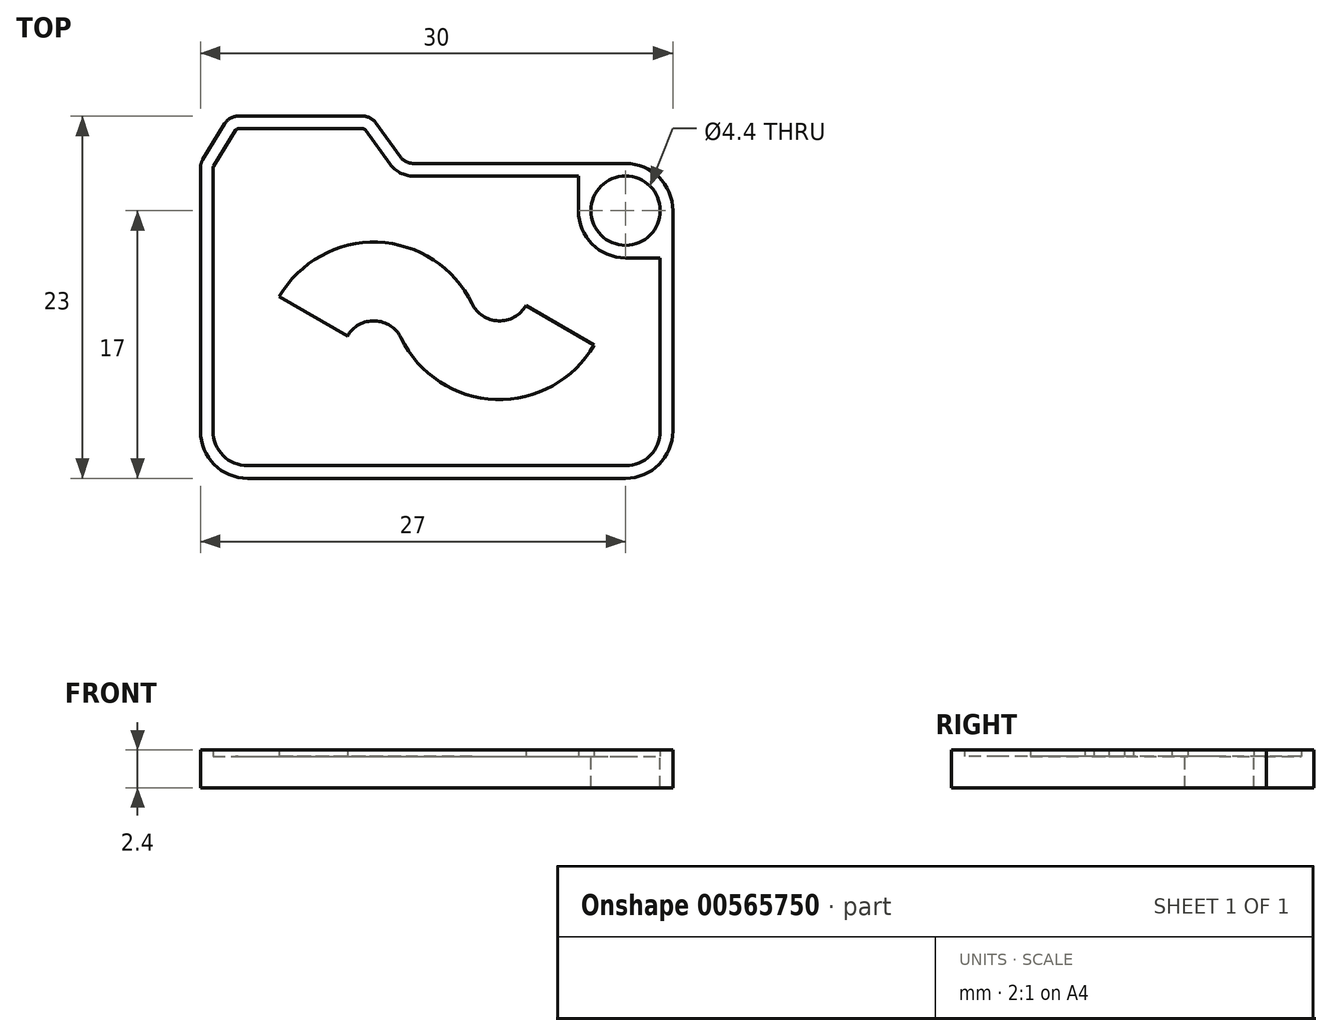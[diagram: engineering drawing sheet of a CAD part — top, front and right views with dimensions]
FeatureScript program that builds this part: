
annotation { "Feature Type Name" : "Feature", "Feature Type Description" : "" }
export const myFeature = defineFeature(function(context is Context, id is Id, definition is map)
    precondition{}
    {
        {
            var Q0;
            Q0=qCreatedBy(makeId("Top.planeOp"),FACE);
            var sketch = newSketch(context, id + "F0", { "sketchPlane" : qUnion([Q0])});
            skLineSegment(sketch, "E0.bottom", {"start": v(-1.49, 10) * mm, "end": v(12, 10) * mm});
            skLineSegment(sketch, "E0.top", {"start": v(-12, -10) * mm, "end": v(12, -10) * mm});
            skLineSegment(sketch, "E0.left", {"start": v(-15, 9.72) * mm, "end": v(-15, -7) * mm});
            skLineSegment(sketch, "E0.right", {"start": v(15, 7) * mm, "end": v(15, -7) * mm});
            skPoint(sketch, "E0.middle", {"position": v(0, 0) * mm});
            skLineSegment(sketch, "E1", {"start": v(-14.85, 10.24) * mm, "end": v(-13.46, 12.52) * mm});
            skLineSegment(sketch, "E2", {"start": v(-12.6, 13) * mm, "end": v(-4.68, 13) * mm});
            skLineSegment(sketch, "E3", {"start": v(-3.86, 12.58) * mm, "end": v(-2.3, 10.42) * mm});
            skArc(sketch, "E4", {"start": v(-2.25, -1.1) * mm, "mid": v(-3.92, 0) * mm, "end": v(-5.67, -0.97) * mm});
            skArc(sketch, "E5", {"start": v(2.25, 1.1) * mm, "mid": v(-3.74, 5) * mm, "end": v(-10, 1.53) * mm});
            skArc(sketch, "E6", {"start": v(-2.25, -1.1) * mm, "mid": v(3.74, -5) * mm, "end": v(10, -1.53) * mm});
            skArc(sketch, "E7", {"start": v(2.25, 1.1) * mm, "mid": v(3.92, 0) * mm, "end": v(5.67, 0.97) * mm});
            skLineSegment(sketch, "E8", {"start": v(-5.67, -0.97) * mm, "end": v(-10, 1.53) * mm});
            skLineSegment(sketch, "E9", {"start": v(5.67, 0.97) * mm, "end": v(10, -1.53) * mm});
            skPoint(sketch, "E10.visualSharp", {"position": v(15, 10) * mm});
            skArc(sketch, "E10.filletArc", {"start": v(15, 7) * mm, "mid": v(14.12, 9.12) * mm, "end": v(12, 10) * mm});
            skPoint(sketch, "E11.visualSharp", {"position": v(15, -10) * mm});
            skArc(sketch, "E11.filletArc", {"start": v(12, -10) * mm, "mid": v(14.12, -9.12) * mm, "end": v(15, -7) * mm});
            skPoint(sketch, "E12.visualSharp", {"position": v(-15, -10) * mm});
            skArc(sketch, "E12.filletArc", {"start": v(-15, -7) * mm, "mid": v(-14.12, -9.12) * mm, "end": v(-12, -10) * mm});
            skPoint(sketch, "E13.visualSharp", {"position": v(-15, 10) * mm});
            skArc(sketch, "E13.filletArc", {"start": v(-14.85, 10.24) * mm, "mid": v(-14.96, 9.99) * mm, "end": v(-15, 9.72) * mm});
            skPoint(sketch, "E14.visualSharp", {"position": v(-2, 10) * mm});
            skArc(sketch, "E14.filletArc", {"start": v(-2.3, 10.42) * mm, "mid": v(-1.94, 10.1) * mm, "end": v(-1.49, 10) * mm});
            skPoint(sketch, "E15.visualSharp", {"position": v(-4.16, 13) * mm});
            skArc(sketch, "E15.filletArc", {"start": v(-3.86, 12.58) * mm, "mid": v(-4.22, 12.9) * mm, "end": v(-4.68, 13) * mm});
            skPoint(sketch, "E16.visualSharp", {"position": v(-13.16, 13) * mm});
            skArc(sketch, "E16.filletArc", {"start": v(-12.6, 13) * mm, "mid": v(-13.1, 12.87) * mm, "end": v(-13.46, 12.52) * mm});
            skLineSegment(sketch, "E17", {"start": v(-2.25, -1.1) * mm, "end": v(2.25, 1.1) * mm, "construction": true});
            skArc(sketch, "E18.0", {"start": v(-14.17, 9.82) * mm, "mid": v(-14.2, 9.77) * mm, "end": v(-14.2, 9.72) * mm});
            skLineSegment(sketch, "E18.1", {"start": v(-14.2, 9.72) * mm, "end": v(-14.2, -7) * mm});
            skArc(sketch, "E18.2", {"start": v(-14.2, -7) * mm, "mid": v(-13.56, -8.56) * mm, "end": v(-12, -9.2) * mm});
            skLineSegment(sketch, "E18.3", {"start": v(-4.51, 12.12) * mm, "end": v(-2.95, 9.95) * mm});
            skArc(sketch, "E18.4", {"start": v(-4.51, 12.12) * mm, "mid": v(-4.58, 12.18) * mm, "end": v(-4.68, 12.2) * mm});
            skLineSegment(sketch, "E18.5", {"start": v(-12.6, 12.2) * mm, "end": v(-4.68, 12.2) * mm});
            skArc(sketch, "E18.6", {"start": v(-12.6, 12.2) * mm, "mid": v(-12.7, 12.17) * mm, "end": v(-12.77, 12.1) * mm});
            skArc(sketch, "E18.7", {"start": v(-2.95, 9.95) * mm, "mid": v(-2.3, 9.4) * mm, "end": v(-1.49, 9.2) * mm});
            skLineSegment(sketch, "E18.8", {"start": v(-1.49, 9.2) * mm, "end": v(9, 9.2) * mm});
            skLineSegment(sketch, "E18.10", {"start": v(-14.17, 9.82) * mm, "end": v(-12.77, 12.1) * mm});
            skLineSegment(sketch, "E18.11", {"start": v(14.2, 4) * mm, "end": v(14.2, -7) * mm});
            skArc(sketch, "E18.12", {"start": v(12, -9.2) * mm, "mid": v(13.56, -8.56) * mm, "end": v(14.2, -7) * mm});
            skLineSegment(sketch, "E18.13", {"start": v(-12, -9.2) * mm, "end": v(12, -9.2) * mm});
            skCircle(sketch, "E19", {"center": v(12, 7) * mm, "radius": 2.2 * mm});
            skArc(sketch, "E20", {"start": v(12, 4) * mm, "mid": v(9.88, 4.88) * mm, "end": v(9, 7) * mm});
            skLineSegment(sketch, "E21", {"start": v(9, 7) * mm, "end": v(9, 9.2) * mm});
            skLineSegment(sketch, "E22", {"start": v(12, 4) * mm, "end": v(14.2, 4) * mm});
            skSolve(sketch);
        }
        {
            var Q0;
            Q0=makeQuery(id+"F0.imprint","IMPRINT",FACE,{"disambiguationData":[TD([[makeQuery(id+"F0.imprint","IMPRINT",EDGE,{"derivedFrom":sQuery(id+"F0.wireOp",EDGE,"E0.bottom")}),-1.0]])]});
            var Q1;
            Q1=makeQuery(id+"F0.imprint","IMPRINT",FACE,{"disambiguationData":[TD([[makeQuery(id+"F0.imprint","IMPRINT",EDGE,{"derivedFrom":sQuery(id+"F0.wireOp",EDGE,"E4")}),-1.0]])]});
            var Q2;
            Q2=makeQuery(id+"F0.imprint","IMPRINT",FACE,{"disambiguationData":[TD([[makeQuery(id+"F0.imprint","IMPRINT",EDGE,{"derivedFrom":sQuery(id+"F0.wireOp",EDGE,"E4")}),1.0]])]});
            extrude(context, id + "F1", {"entities" : qUnion([Q0, Q1, Q2]), "oppositeDirection" : true, "depth" : 2 * mm, "offsetDistance" : 25 * mm});
        }
        {
            var Q0;
            Q0=makeQuery(id+"F0.imprint","IMPRINT",FACE,{"disambiguationData":[TD([[makeQuery(id+"F0.imprint","IMPRINT",EDGE,{"derivedFrom":sQuery(id+"F0.wireOp",EDGE,"E4")}),-1.0]])]});
            var Q1;
            Q1=makeQuery(id+"F0.imprint","IMPRINT",FACE,{"disambiguationData":[TD([[makeQuery(id+"F0.imprint","IMPRINT",EDGE,{"derivedFrom":sQuery(id+"F0.wireOp",EDGE,"E0.bottom")}),-1.0]])]});
            extrude(context, id + "F2", {"entities" : qUnion([Q0, Q1]), "operationType" : NewBodyOperationType.ADD, "depth" : 0.4 * mm, "offsetDistance" : 25 * mm});
        }
    });
